# Revit family: Geberit DuofixBasic element za konzolnu WC šolju, 112 cm, sa Delta ugradnim vodokotlićem 12 cm_PRO_101049
name_source: partatom
category: Plumbing Fixtures
revit_build: Autodesk Revit 2018 (Build: 20190510_1515(x64)
units: mm (PartAtom-declared; Revit-internal decimal feet)

## family parameters
Always vertical = Yes
Cut with Voids When Loaded = No
OmniClass Number = 23.45.05.00
OmniClass Title = Sanitary Equipment
Part Type = Normal
Room Calculation Point = Yes
Round Connector Dimension = Use Diameter
Shared = No
Work Plane-Based = No

## types (1)
- 458.103.00.1 Geberit DuofixBasic element za konzolnu WC šolju, 112 cm, sa Delta ugradnim vodokotlićem 12 cm
    ATT_11256 = 12 St.
    ATT_11257 = 60 St.
    ATT_11258 = 120 St.
    ATT_11259 = 240 St.
    BIM datoteka, datum izmene = 2021.12.01
    BIM datoteka, proizvođač = Geberit
    BIM datoteka, verzija = GEB MG 1.5
    Broj artikla = 458.103.00.1
    CW Connection = Yes
    D = 170 mm  [stored 0.557743 ft]
    D1 = 60 mm  [stored 0.19685 ft]
    Description = Geberit DuofixBasic element za konzolnu WC šolju, 112 cm, sa Delta ugradnim vodokotlićem 12 cm
    EAN code basic data = 4025416758877
    Fabrički podešena količina ispiranja = 6 i 3 l
    GEB_culture = sr-RS
    GEB_generic_description = concealed cistern support frame for toilet
    GEB_generic_manufacturer = generic
    GEB_imperial_engineering = No
    GEB_metric_engineering = Yes
    GEB_pimversion = 22.02.12
    GEB_processing_type = T
    GEB_reference = PRO_101049
    GEB_translations = {"ATT_10673":"EAN code basic data","ATT_10807":"Opseg podešavanje veće količine vode za ispiranje","ATT_10811":"Opseg podešavanja manje količine vode za ispiranje","ATT_10832":"Maksimalna temperatura vode","ATT_10847":"Minimalni protočni pritisak za izračunati protok","ATT_10866":"Fabrički podešena količina ispiranja","applicationPurposes":"Namene","application_range":"Oblast primene","brandName":"Robna marka","characteristics":"Svojstva","connection_description1":"Opis priključka 1","connection_description2":"Opis priključka 2","GEB_connection_diameter1":"Prečnik priključka 1","GEB_connection_diameter2":"Prečnik priključka 2","connection_type_c01":"Vrsta priključka kod priključka 01","connection_type_c02":"Vrsta priključka kod priključka 02","content_creator":"BIM datoteka, proizvođač","content_date_changed":"BIM datoteka, datum izmene","content_version":"BIM datoteka, verzija","key 1000":"Broj artikla","name":"Naziv","productBrand":"Robna marka proizvoda","scopeOfDelivery":"Obim isporuke","type":"Tip","GEB_cut_length_c01":"Maksimalno skraćenje kod priključka 01","angle":"ugao","placement finished floor":"Na gornjoj ivici gotovog poda","rod spacing 180mm":"Razmak kačenja 180 mm","rod spacing 230mm":"Razmak kačenja 230 mm","sanitary socket":"Spojnica za prelaz","surface height":"Visina debljine poda","warning":"Upozorenje","ATT_10767":"Izračunati protok","fixed_material_01":"Osnovni materijal 01","fixed_material_02":"Osnovni materijal 02","fixed_material_03":"Osnovni materijal 03","fixed_material_04":"Osnovni materijal 04","fixed_material":"Osnovni materijal"}
    GEB_use_DN = Yes
    H = 1120 mm  [stored 3.67454 ft]
    H1 = 230 mm  [stored 0.754593 ft]
    H2 = 330 mm
    H3 = 1000 mm  [stored 3.28084 ft]
    HW Connection = No
    IfcDescription = Geberit DuofixBasic element za konzolnu WC šolju, 112 cm, sa Delta ugradnim vodokotlićem 12 cm
    IfcExportAs = IfcSanitaryTerminal
    IfcExportType = CISTERN
    Izračunati protok = 0.1 L/s
    LOD300 = No
    LOD400 = Yes
    Maksimalna temperatura vode = 25 °C
    Manufacturer = Geberit
    Minimalni protočni pritisak za izračunati protok = 0.5 bar
    Model = Delta 12 cm
    Namene = Za suvu gradnju
Za ugradnju u predzidne konstrukcije delimične ili visine etaže
Za ugradnju u instalacione zidove u visini etaže
Za konzolne WC šolje sa priključnim dimenzijama prema propisu EN 33:2011
Za konzolne WC šolje sa projektovanom dužinom do 62 cm
Za jednokoličinsko, dvokoličinsko ili start/stop ispiranje
Za debljine poda 0–20 cm
    Naziv = Geberit DuofixBasic element za konzolnu WC šolju, 112 cm, sa Delta ugradnim vodokotlićem 12 cm
    Obim isporuke = Ugaoni ventil R 1/2", kompatibilan sa MF adapterom, sa priključnim prstenom
Građevinska zaštita za revizioni otvor, od polistiren pene
2 vijka za okvir tipke
2 zidna sidra
Priključni set za WC, ø 90 mm
Priključno koleno 90° od PE-HD, ø 90 mm
Spojnica za prelaz od PE-HD, ø 90 / 110 mm
2 zaštitna čepa
Traverza za podmetač za oblogu
2 navojne šipke M12
Materijal za pričvršćivanje
    Oblast primene = sanitary systems
    Opis priključka 1 = cold water in
    Opis priključka 2 = sanitary out
    Opseg podešavanja manje količine vode za ispiranje = 3-4 l
    Opseg podešavanje veće količine vode za ispiranje = 4.5 / 6 / 7.5 l
    Osnovni materijal = Geberit, Plastic, Opaque white
    Osnovni materijal 01 = Geberit, Steel, Paint Finish, Blue
    Osnovni materijal 02 = Geberit, Laminate, Ivory, Matte
    Osnovni materijal 03 = Geberit, Steel, galvanized
    Osnovni materijal 04 = Geberit, PE-HD, Black
    Prečnik priključka 1 = 15 mm  [stored 0.0492126 ft]
    Prečnik priključka 2 = 90 mm  [stored 0.295276 ft]
    Robna marka = Geberit
    Robna marka proizvoda = DuofixBasic
    Spojnica za prelaz = No
    Svojstva = Samonoseći okvir sa završnom obradom pečenim lakom
Okvir gore, otvoren
Okvir sa rupama ø 9 mm za učvršćenje u konstrukciji od drvenih okvira
Okvir sa prihvatnim otvorima za Geberit Duofix zidno sidro za elemente sa otvorenim okvirom gore
Pripremljen okvir za podupirače kod WC keramike sa malom oslonom površinom
Potporne noge pocinkovane
Potporne noge, podesive od 0–20 cm
Ploče stope od plastike
Dubina ploče stope odgovara za ugradnju u U-profile UW 50
Priključno koleno koje se može montirati bez alata
Ugradni vodokotlić sa aktiviranjem sa prednje strane
Ugradni vodokotlić sa izolacijom protiv kondenzacije
Kod fabričkog podešavanja moguće je automatsko naknadno ispiranje
Priključak za vodu, pozadi ili gore na sredini
Opremljen praznom cevi za dovod vode ka priključku Geberit AquaClean uređaja za WC tuš
Sa mogućnošću učvršćenja za priključak električnog napajanja
    Tip = Delta 12 cm
    Vent Connection = No
    Vrsta priključka kod priključka 01 = Rp½''
    Vrsta priključka kod priključka 02 = DN90/ø90 Spigot
    W = 500 mm  [stored 1.64042 ft]
    Waste Connection = Yes
    Z2_calculated = 226 mm  [stored 0.74147 ft]
    angle_cw = 90.00°
    button_depth = 115 mm  [stored 0.377297 ft]
    cistern_front_offset = 21 mm  [stored 0.0688976 ft]
    cistern_width = 420 mm  [stored 1.37795 ft]
    connection_bend = Yes
    cw_orientation = 1
    cw_pos = 200 mm  [stored 0.656168 ft]
    frame_btm = 1039 mm  [stored 3.40879 ft]
    h1 = 504 mm  [stored 1.65354 ft]
    outlet_flow = 0.0 L/s
    rod_width_180 = 180 mm  [stored 0.590551 ft]
    rod_width_230 = 230 mm  [stored 0.754593 ft]
    supply_connection_warning = Reducer connected to element not required and should not be accounted for in a BOM
    wt_h = 41 mm  [stored 0.134514 ft]

note: [stored X ft] marks values corroborated as IEEE doubles in the binary element streams (Revit-internal decimal feet)

## geometry (parser evidence)
native form markers: Blend x6, Sweep x2
no freeform markers — native parametric forms only
